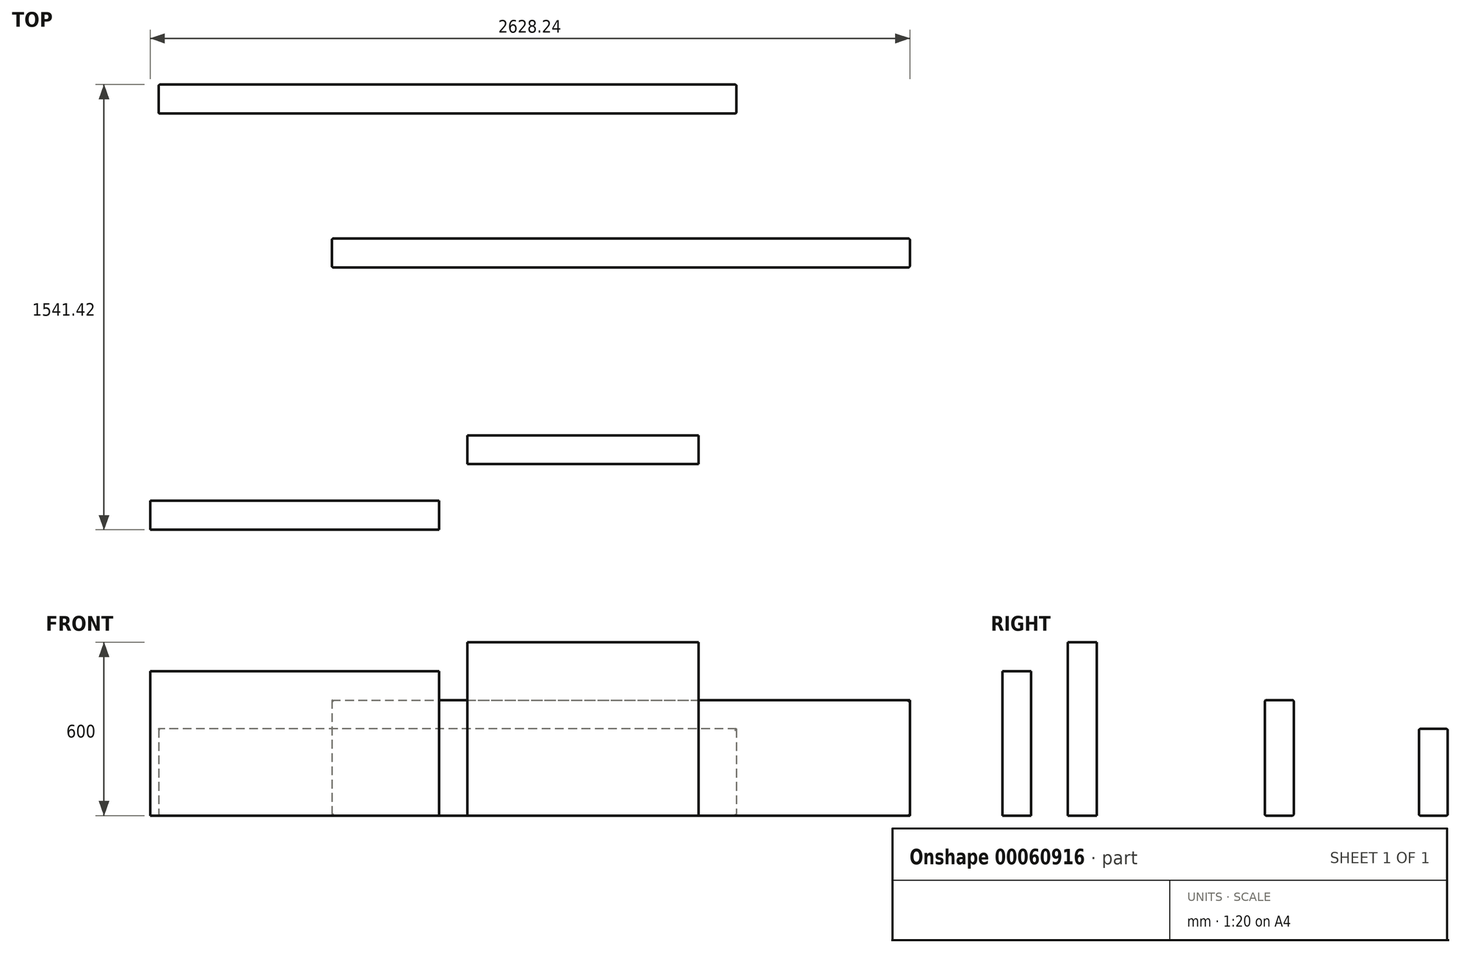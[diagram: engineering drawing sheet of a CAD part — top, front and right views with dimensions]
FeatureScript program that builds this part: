
annotation { "Feature Type Name" : "Feature", "Feature Type Description" : "" }
export const myFeature = defineFeature(function(context is Context, id is Id, definition is map)
    precondition{}
    {
        {
            var Q0;
            Q0=qCreatedBy(makeId("Top.planeOp"),FACE);
            var sketch = newSketch(context, id + "F0", { "sketchPlane" : qUnion([Q0])});
            skLineSegment(sketch, "E0.rect.bottom", {"start": v(1000, -50) * mm, "end": v(-1000, -50) * mm});
            skLineSegment(sketch, "E0.rect.top", {"start": v(1000, 50) * mm, "end": v(-1000, 50) * mm});
            skLineSegment(sketch, "E0.rect.left", {"start": v(1000, -50) * mm, "end": v(1000, 50) * mm});
            skLineSegment(sketch, "E0.rect.right", {"start": v(-1000, -50) * mm, "end": v(-1000, 50) * mm});
            skPoint(sketch, "E0.rect.middle", {"position": v(0, 0) * mm});
            skSolve(sketch);
        }
        {
            var Q0;
            Q0 = qSketchRegion(id + "F0", true);
            extrude(context, id + "F1", {"entities" : qUnion([Q0]), "depth" : 300 * mm});
        }
        {
            var Q0;
            Q0=makeQuery(id+"F1.opExtrude","SWEPT_FACE",FACE,{"disambiguationData":[OSD([sQuery(id+"F0.wireOp",EDGE,"E0.rect.bottom")])]});
            var Q1;
            Q1=makeQuery(id+"F1.opExtrude","SWEPT_FACE",FACE,{"disambiguationData":[OSD([sQuery(id+"F0.wireOp",EDGE,"E0.rect.top")])]});
            fillet(context, id + "F2", {"entities" : qUnion([Q0, Q1]), "radius" : 5 * mm, "tangentPropagation" : true, "allowEdgeOverflow" : false});
        }
        {
            var Q0;
            Q0=qCreatedBy(makeId("Top.planeOp"),FACE);
            var sketch = newSketch(context, id + "F3", { "sketchPlane" : qUnion([Q0])});
            skLineSegment(sketch, "E1.bottom", {"start": v(-400.23, -483.03) * mm, "end": v(1599.77, -483.03) * mm});
            skLineSegment(sketch, "E1.top", {"start": v(-400.23, -583.03) * mm, "end": v(1599.77, -583.03) * mm});
            skLineSegment(sketch, "E1.left", {"start": v(-400.23, -483.03) * mm, "end": v(-400.23, -583.03) * mm});
            skLineSegment(sketch, "E1.right", {"start": v(1599.77, -483.03) * mm, "end": v(1599.77, -583.03) * mm});
            skSolve(sketch);
        }
        {
            var Q0;
            Q0 = qSketchRegion(id + "F3", true);
            extrude(context, id + "F4", {"entities" : qUnion([Q0]), "depth" : 400 * mm});
        }
        {
            var Q0;
            Q0=makeQuery(id+"F4.opExtrude","SWEPT_FACE",FACE,{"disambiguationData":[OSD([sQuery(id+"F3.wireOp",EDGE,"E1.top")])]});
            var Q1;
            Q1=makeQuery(id+"F4.opExtrude","SWEPT_FACE",FACE,{"disambiguationData":[OSD([sQuery(id+"F3.wireOp",EDGE,"E1.bottom")])]});
            fillet(context, id + "F5", {"entities" : qUnion([Q0, Q1]), "radius" : 5 * mm, "tangentPropagation" : true, "allowEdgeOverflow" : false});
        }
        {
            var Q0;
            Q0=qCreatedBy(makeId("Top.planeOp"),FACE);
            var sketch = newSketch(context, id + "F6", { "sketchPlane" : qUnion([Q0])});
            skLineSegment(sketch, "E2.bottom", {"start": v(68.44, -1164.4) * mm, "end": v(868.44, -1164.4) * mm});
            skLineSegment(sketch, "E2.top", {"start": v(68.44, -1264.4) * mm, "end": v(868.44, -1264.4) * mm});
            skLineSegment(sketch, "E2.left", {"start": v(68.44, -1164.4) * mm, "end": v(68.44, -1264.4) * mm});
            skLineSegment(sketch, "E2.right", {"start": v(868.44, -1164.4) * mm, "end": v(868.44, -1264.4) * mm});
            skSolve(sketch);
        }
        {
            var Q0;
            Q0=makeQuery(id+"F6.imprint","IMPRINT",FACE,{"disambiguationData":[TD([[makeQuery(id+"F6.imprint","IMPRINT",EDGE,{"derivedFrom":sQuery(id+"F6.wireOp",EDGE,"E2.bottom")}),-1.0]])]});
            extrude(context, id + "F7", {"entities" : qUnion([Q0]), "depth" : 600 * mm});
        }
        {
            var Q0;
            Q0=qCreatedBy(makeId("Top.planeOp"),FACE);
            var sketch = newSketch(context, id + "F8", { "sketchPlane" : qUnion([Q0])});
            skLineSegment(sketch, "E3.bottom", {"start": v(-1028.47, -1391.42) * mm, "end": v(-28.47, -1391.42) * mm});
            skLineSegment(sketch, "E3.top", {"start": v(-1028.47, -1491.42) * mm, "end": v(-28.47, -1491.42) * mm});
            skLineSegment(sketch, "E3.left", {"start": v(-1028.47, -1391.42) * mm, "end": v(-1028.47, -1491.42) * mm});
            skLineSegment(sketch, "E3.right", {"start": v(-28.47, -1391.42) * mm, "end": v(-28.47, -1491.42) * mm});
            skSolve(sketch);
        }
        {
            var Q0;
            Q0 = qSketchRegion(id + "F8", true);
            extrude(context, id + "F9", {"entities" : qUnion([Q0]), "depth" : 500 * mm});
        }
    });
